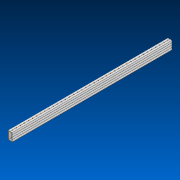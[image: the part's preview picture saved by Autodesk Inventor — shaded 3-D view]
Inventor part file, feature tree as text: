
AUTODESK INVENTOR PART (.ipt)
format: ipt  version: 2022.2 (Build 262287000, 287)  size: 541,696 bytes
history: native  units: in
note: dims shown in document units (in); Inventor stores cm internally (conversion verified against a paired STEP export)
features: other x40, extrude x1, pattern_linear x1, sketch x1
ambient origin geometry x8: Origin, YZ Plane, XZ Plane, XY Plane, X Axis, Y Axis, Z Axis, Center Point
bodies: Solid1 (feature_tree)
feature tree (43):
  extrude  "Extrusion1"  Depth=2.0in
  other  "Work Axis1"
  pattern_linear  "Rectangular Pattern1"  Spacing1=20.0in  [1 undecoded]
  sketch  "Sketch1"  dims[d0=1.0in d1=2.0in d2=20.0in d3=0.0in d4=15.3543in d6=1.0in]
  other  "Work Axis2"
  other  "Work Axis3"
  other  "Work Axis4"
  other  "Work Axis5"
  other  "Work Axis6"
  other  "Work Axis7"
  other  "Work Axis8"
  other  "Work Axis9"
  other  "Work Axis10"
  other  "Work Axis60"
  other  "Work Axis61"
  other  "Work Axis62"
  other  "Work Axis63"
  other  "Work Axis64"
  other  "Work Axis65"
  other  "Work Axis66"
  other  "Work Axis67"
  other  "Work Axis68"
  other  "Work Axis69"
  other  "Work Axis70"
  other  "Work Axis71"
  other  "Work Axis72"
  other  "Work Axis73"
  other  "Work Axis74"
  other  "Work Axis75"
  other  "Work Axis76"
  other  "Work Axis77"
  other  "Work Axis78"
  other  "Work Axis79"
  other  "Work Axis80"
  other  "Work Axis81"
  other  "Work Axis82"
  other  "Work Axis83"
  other  "Work Axis84"
  other  "Work Axis85"
  other  "Work Axis86"
  other  "Work Axis87"
  other  "Work Axis88"
  other  "Cut-Extrude2"
note: 1 required parameter value undecoded (feature->parameter linkage not recoverable at this tier; creation-order binding heuristic only, values carry confidence <= 0.55)
